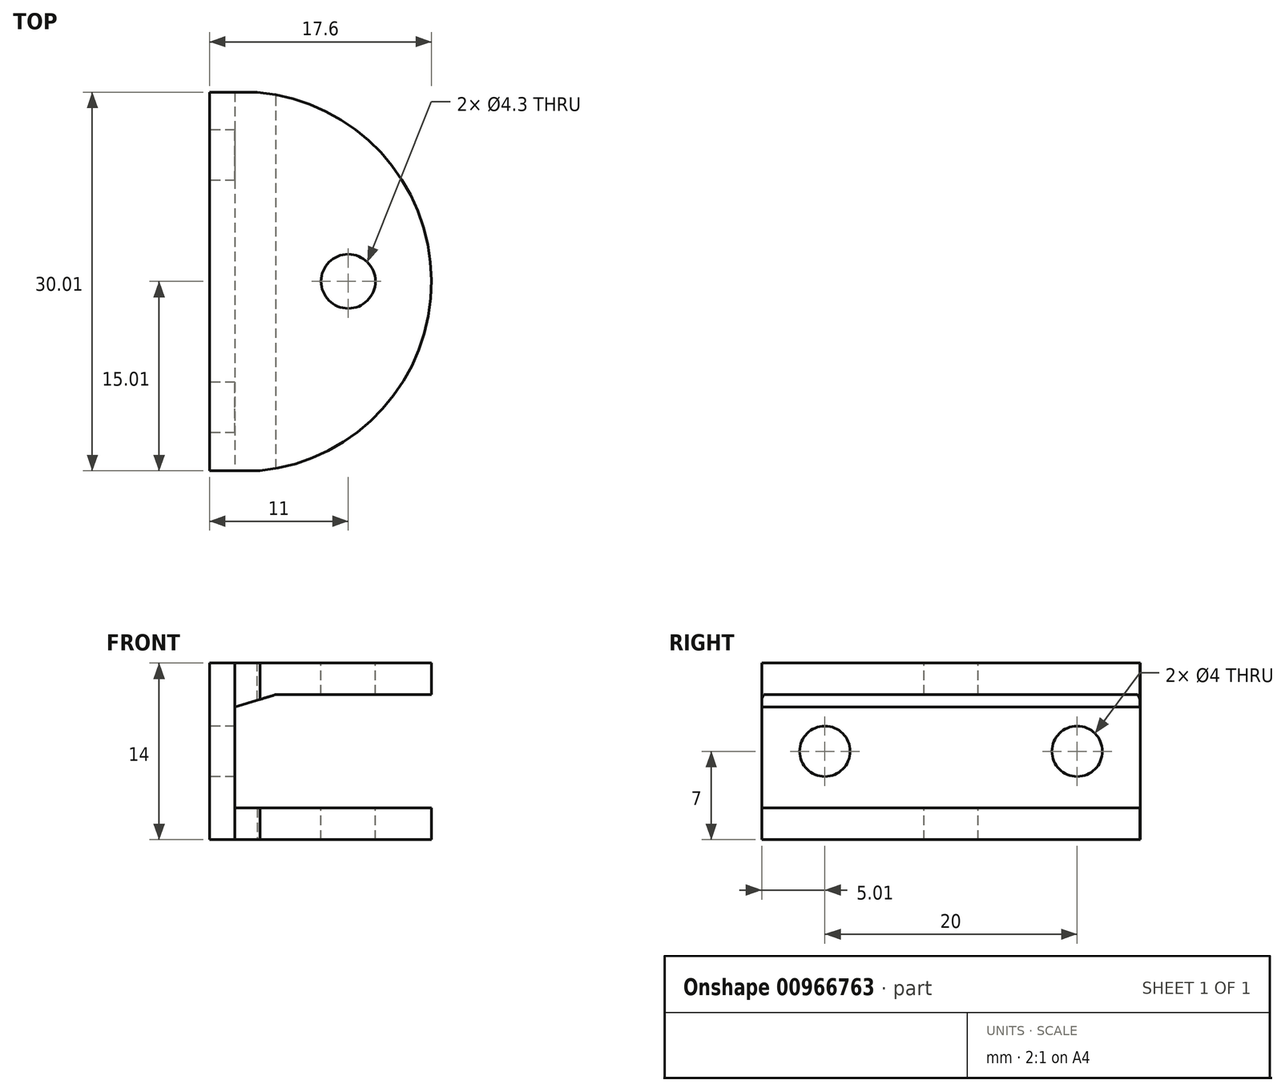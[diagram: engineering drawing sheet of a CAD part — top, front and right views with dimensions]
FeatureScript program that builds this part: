
annotation { "Feature Type Name" : "Feature", "Feature Type Description" : "" }
export const myFeature = defineFeature(function(context is Context, id is Id, definition is map)
    precondition{}
    {
        {
            var Q0;
            Q0=qCreatedBy(makeId("Right.planeOp"),FACE);
            var sketch = newSketch(context, id + "F0", { "sketchPlane" : qUnion([Q0])});
            skLineSegment(sketch, "E0.bottom", {"start": v(15, -7) * mm, "end": v(-15, -7) * mm});
            skLineSegment(sketch, "E0.top", {"start": v(15, 7) * mm, "end": v(-15, 7) * mm});
            skLineSegment(sketch, "E0.left", {"start": v(15, -7) * mm, "end": v(15, 7) * mm});
            skLineSegment(sketch, "E0.right", {"start": v(-15, -7) * mm, "end": v(-15, 7) * mm});
            skPoint(sketch, "E0.middle", {"position": v(0, 0) * mm});
            skCircle(sketch, "E1", {"center": v(10, 0) * mm, "radius": 2 * mm});
            skCircle(sketch, "E2.MirrorC", {"center": v(-10, 0) * mm, "radius": 2 * mm});
            skSolve(sketch);
        }
        {
            var Q0;
            Q0=makeQuery(id+"F0.imprint","IMPRINT",FACE,{"disambiguationData":[TD([[makeQuery(id+"F0.imprint","IMPRINT",EDGE,{"derivedFrom":sQuery(id+"F0.wireOp",EDGE,"E0.bottom")}),-1.0]])]});
            extrude(context, id + "F1", {"entities" : qUnion([Q0]), "depth" : 2 * mm, "offsetDistance" : 25 * mm});
        }
        {
            var Q0;
            Q0=makeQuery(id+"F1.opExtrude","SWEPT_FACE",FACE,{"disambiguationData":[OSD([sQuery(id+"F0.wireOp",EDGE,"E0.top")])]});
            cPlane(context, id + "F2", {"entities" : qUnion([Q0]), "cplaneType" : CPlaneType.OFFSET, "offset" : 0 * mm, "width" : 150 * mm, "height" : 150 * mm});
        }
        {
            var Q0;
            Q0=qCreatedBy(id+"F2.planeOp",FACE);
            var sketch = newSketch(context, id + "F3", { "sketchPlane" : qUnion([Q0])});
            skLineSegment(sketch, "E3", {"start": v(3.8, 14.99) * mm, "end": v(0, 14.99) * mm});
            skLineSegment(sketch, "E4", {"start": v(0, 14.99) * mm, "end": v(0, -14.99) * mm});
            skLineSegment(sketch, "E5", {"start": v(0, -14.99) * mm, "end": v(4, -15.01) * mm});
            skArc(sketch, "E6", {"start": v(4, -15.01) * mm, "mid": v(17.6, 0.08) * mm, "end": v(3.8, 14.99) * mm});
            skSolve(sketch);
        }
        {
            var Q0;
            Q0=makeQuery(id+"F3.imprint","IMPRINT",FACE,{"disambiguationData":[TD([[makeQuery(id+"F3.imprint","IMPRINT",EDGE,{"derivedFrom":sQuery(id+"F3.wireOp",EDGE,"E3")}),1.0]])]});
            extrude(context, id + "F4", {"entities" : qUnion([Q0]), "operationType" : NewBodyOperationType.ADD, "oppositeDirection" : true, "depth" : 2.5 * mm, "offsetDistance" : 25 * mm});
        }
        {
            var Q0;
            Q0=makeQuery(id+"F1.opExtrude","SWEPT_BODY",BODY,{"disambiguationData":[OSD([sQuery(id+"F0.wireOp",EDGE,"E0.bottom"),sQuery(id+"F0.wireOp",EDGE,"E0.top"),sQuery(id+"F0.wireOp",EDGE,"E0.left"),sQuery(id+"F0.wireOp",EDGE,"E0.right"),sQuery(id+"F0.wireOp",EDGE,"E1"),sQuery(id+"F0.wireOp",EDGE,"E2.MirrorC")])]});
            var Q1;
            Q1=qCreatedBy(makeId("Top.planeOp"),FACE);
            mirror(context, id + "F5", {"operationType" : NewBodyOperationType.ADD, "entities" : qUnion([Q0]), "mirrorPlane" : qUnion([Q1])});
        }
        {
            var Q0;
            Q0=makeQuery(id+"F4.boolean.opBoolean","INTERSECT",EDGE,{"derivedFrom":[makeQuery(id+"F1.opExtrude","CAP_FACE",FACE,{"disambiguationData":[OSD([sQuery(id+"F0.wireOp",EDGE,"E0.bottom"),sQuery(id+"F0.wireOp",EDGE,"E0.top"),sQuery(id+"F0.wireOp",EDGE,"E0.left"),sQuery(id+"F0.wireOp",EDGE,"E0.right"),sQuery(id+"F0.wireOp",EDGE,"E1"),sQuery(id+"F0.wireOp",EDGE,"E2.MirrorC")])],"isStart":false}),makeQuery(id+"F4.opExtrude","CAP_FACE",FACE,{"disambiguationData":[OSD([sQuery(id+"F3.wireOp",EDGE,"618f8162-c980-41b0-ba47-ffeaf294494b"),sQuery(id+"F3.wireOp",EDGE,"E3"),sQuery(id+"F3.wireOp",EDGE,"E4"),sQuery(id+"F3.wireOp",EDGE,"E5"),sQuery(id+"F3.wireOp",EDGE,"iB8eIBPW-2yHO-Ouch-LAX0-gYp5qs3KyxpB")])],"isStart":false})]});
            var Q1;
            Q1=makeQuery(id+"F5.opPattern","COPY",EDGE,{"derivedFrom":makeQuery(id+"F4.boolean.opBoolean","INTERSECT",EDGE,{"derivedFrom":[makeQuery(id+"F1.opExtrude","CAP_FACE",FACE,{"disambiguationData":[OSD([sQuery(id+"F0.wireOp",EDGE,"E0.bottom"),sQuery(id+"F0.wireOp",EDGE,"E0.top"),sQuery(id+"F0.wireOp",EDGE,"E0.left"),sQuery(id+"F0.wireOp",EDGE,"E0.right"),sQuery(id+"F0.wireOp",EDGE,"E1"),sQuery(id+"F0.wireOp",EDGE,"E2.MirrorC")])],"isStart":false}),makeQuery(id+"F4.opExtrude","CAP_FACE",FACE,{"disambiguationData":[OSD([sQuery(id+"F3.wireOp",EDGE,"618f8162-c980-41b0-ba47-ffeaf294494b"),sQuery(id+"F3.wireOp",EDGE,"E3"),sQuery(id+"F3.wireOp",EDGE,"E4"),sQuery(id+"F3.wireOp",EDGE,"E5"),sQuery(id+"F3.wireOp",EDGE,"iB8eIBPW-2yHO-Ouch-LAX0-gYp5qs3KyxpB")])],"isStart":false})]}),"instanceName":"1"});
            chamfer(context, id + "F6", {"entities" : qUnion([Q0, Q1]), "chamferType" : ChamferType.OFFSET_ANGLE, "width" : 1 * mm, "oppositeDirection" : false, "angle" : 73 * degree, "tangentPropagation" : true});
        }
        {
            var Q0;
            Q0=makeQuery(id+"F3.imprint","IMPRINT",FACE,{"disambiguationData":[TD([[makeQuery(id+"F3.imprint","IMPRINT",EDGE,{"derivedFrom":sQuery(id+"F3.wireOp",EDGE,"E3")}),1.0]])]});
            cPlane(context, id + "F7", {"entities" : qUnion([Q0]), "cplaneType" : CPlaneType.OFFSET, "offset" : 0.7 * mm, "width" : 150 * mm, "height" : 150 * mm});
        }
        {
            var Q0;
            Q0=qCreatedBy(id+"F7.planeOp",FACE);
            var sketch = newSketch(context, id + "F8", { "sketchPlane" : qUnion([Q0])});
            skCircle(sketch, "E7", {"center": v(11, 0) * mm, "radius": 2.15 * mm});
            skSolve(sketch);
        }
        {
            var Q0;
            Q0=makeQuery(id+"F8.imprint","IMPRINT",FACE,{"disambiguationData":[TD([[makeQuery(id+"F8.imprint","IMPRINT",EDGE,{"derivedFrom":sQuery(id+"F8.wireOp",EDGE,"E7")}),1.0]])]});
            extrude(context, id + "F9", {"entities" : qUnion([Q0]), "operationType" : NewBodyOperationType.REMOVE, "endBound" : BoundingType.THROUGH_ALL, "oppositeDirection" : true, "depth" : 25 * mm, "offsetDistance" : 25 * mm});
        }
    });
